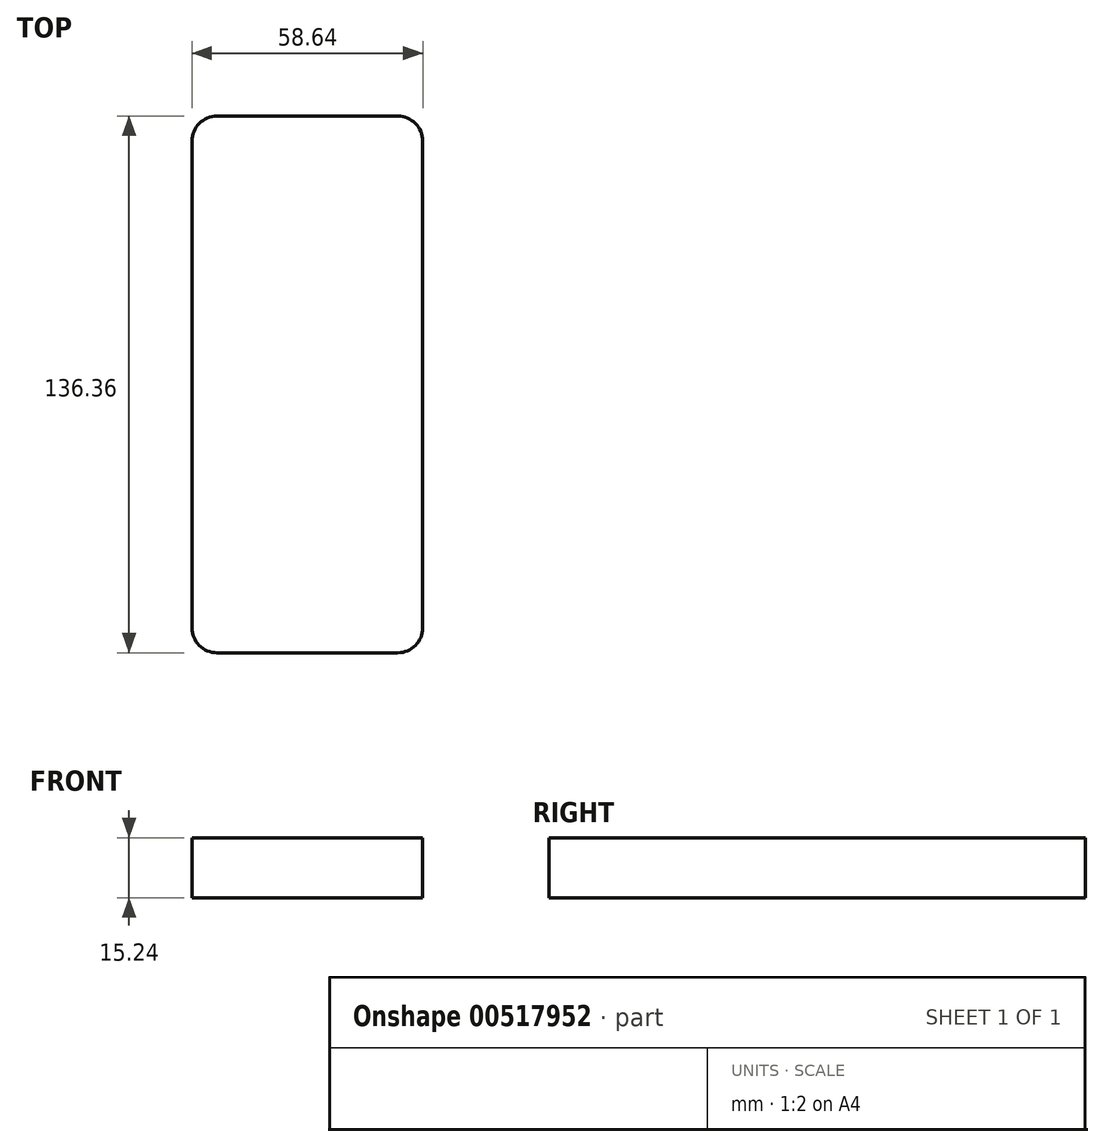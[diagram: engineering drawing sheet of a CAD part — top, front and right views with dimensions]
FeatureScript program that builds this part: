
annotation { "Feature Type Name" : "Feature", "Feature Type Description" : "" }
export const myFeature = defineFeature(function(context is Context, id is Id, definition is map)
    precondition{}
    {
        {
            var Q0;
            Q0=qCreatedBy(makeId("Top.planeOp"),FACE);
            var sketch = newSketch(context, id + "F0", { "sketchPlane" : qUnion([Q0])});
            skLineSegment(sketch, "E0.bottom", {"start": v(-34.98, 68.12) * mm, "end": v(10.96, 68.12) * mm});
            skLineSegment(sketch, "E0.top", {"start": v(-34.98, -68.24) * mm, "end": v(10.96, -68.24) * mm});
            skLineSegment(sketch, "E0.left", {"start": v(-41.33, 61.77) * mm, "end": v(-41.33, -61.89) * mm});
            skLineSegment(sketch, "E0.right", {"start": v(17.3, 61.77) * mm, "end": v(17.3, -61.89) * mm});
            skPoint(sketch, "E1.visualSharp", {"position": v(-41.33, 68.12) * mm});
            skArc(sketch, "E1.filletArc", {"start": v(-34.98, 68.12) * mm, "mid": v(-39.47, 66.26) * mm, "end": v(-41.33, 61.77) * mm});
            skPoint(sketch, "E2.visualSharp", {"position": v(17.3, 68.12) * mm});
            skArc(sketch, "E2.filletArc", {"start": v(17.3, 61.77) * mm, "mid": v(15.45, 66.26) * mm, "end": v(10.96, 68.12) * mm});
            skPoint(sketch, "E3.visualSharp", {"position": v(17.3, -68.24) * mm});
            skArc(sketch, "E3.filletArc", {"start": v(10.96, -68.24) * mm, "mid": v(15.45, -66.38) * mm, "end": v(17.3, -61.89) * mm});
            skPoint(sketch, "E4.visualSharp", {"position": v(-41.33, -68.24) * mm});
            skArc(sketch, "E4.filletArc", {"start": v(-41.33, -61.89) * mm, "mid": v(-39.47, -66.38) * mm, "end": v(-34.98, -68.24) * mm});
            skSolve(sketch);
        }
        {
            var Q0;
            Q0 = qSketchRegion(id + "F0", true);
            extrude(context, id + "F1", {"entities" : qUnion([Q0]), "depth" : 15.24 * mm, "offsetDistance" : 25.4 * mm});
        }
    });
